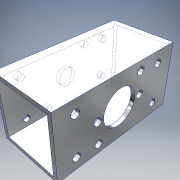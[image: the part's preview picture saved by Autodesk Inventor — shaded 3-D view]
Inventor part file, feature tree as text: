
AUTODESK INVENTOR PART (.ipt)
format: ipt  version: 2019 (Build 230136000, 136)  size: 183,296 bytes
history: native  units: in
note: dims shown in document units (in); Inventor stores cm internally (conversion verified against a paired STEP export)
features: reference x11, extrude x7, sketch x7, other x4
ambient origin geometry x8: Origin, YZ Plane, XZ Plane, XY Plane, X Axis, Y Axis, Z Axis, Center Point
bodies: Solid1 (feature_tree)
feature tree (29):
  extrude  "Extrusion1"  Depth=0.125in
  sketch  "Sketch6"  dims[d2=4.0in d3=0.0in d11=2.0in]
  extrude  "Extrusion8"  Depth=2.0in
  extrude  "Extrusion9"  Depth=0.125in
  extrude  "Extrusion10"  Depth=1.0in TaperAngle=0.0deg
  extrude  "Extrusion11"  Depth=1.0in
  extrude  "Extrusion12"  Depth=1.0in
  extrude  "Extrusion13"  Depth=1.0in
  sketch  "Sketch1"  dims[d0=2.0in d1=0.125in]
  reference  "Reference2"
  sketch  "Sketch7"  dims[d12=0.125in d25=1.125in]
  sketch  "Sketch8"  dims[d26=1.0in d27=0.0in d28=1.0in d29=0.0in]
  reference  "Reference3"
  reference  "Reference4"
  reference  "Reference5"
  reference  "Reference6"
  sketch  "Sketch9"  dims[d30=1.0in d31=0.0in d32=0.25in]
  reference  "Reference7"
  reference  "Reference8"
  reference  "Reference9"
  reference  "Reference10"
  sketch  "Sketch10"  dims[d33=1.0in d34=0.0in d35=0.25in]
  reference  "Reference11"
  reference  "Reference12"
  sketch  "Sketch11"  dims[d36=1.0in d37=0.0in d38=0.19in d39=1.0in d40=0.0in]
  parser-record x1  (decoder bookkeeping rows leaked as tree rows — omitted from the tree; the rows remain in map.json)
  other  "Drive Arm.iam"
  other  "Arm 2 inch A:1"
  other  "Arm 2 inch C:1"
note: 1 file-system path scrubbed to <path> (originals preserved in map.json)
